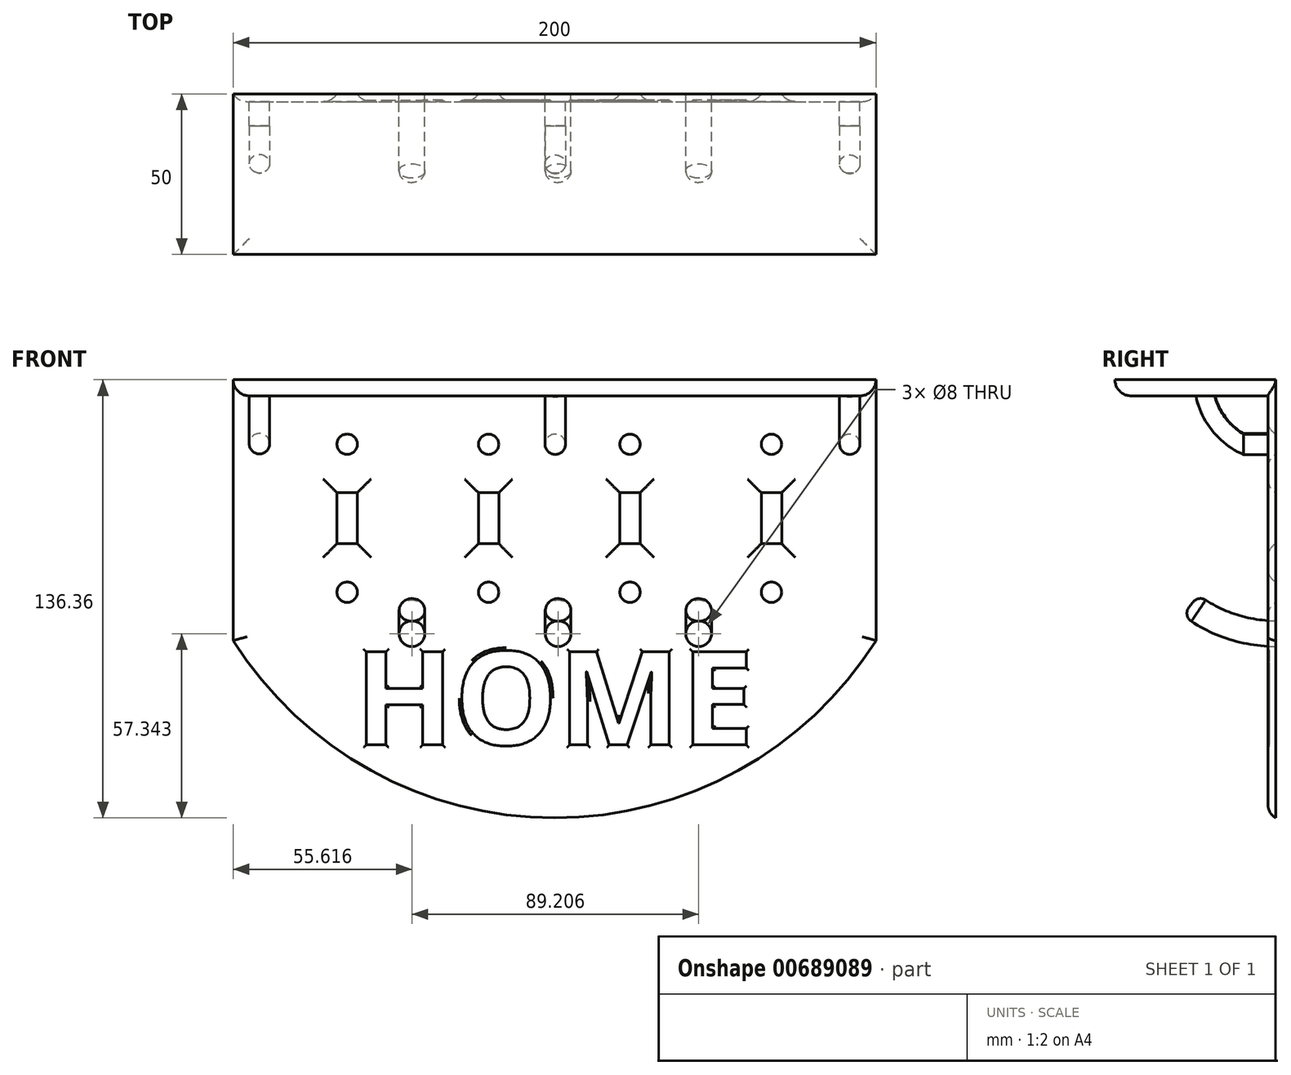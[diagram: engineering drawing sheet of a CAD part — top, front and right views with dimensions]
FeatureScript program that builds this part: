
annotation { "Feature Type Name" : "Feature", "Feature Type Description" : "" }
export const myFeature = defineFeature(function(context is Context, id is Id, definition is map)
    precondition{}
    {
        {
            var Q0;
            Q0=qCreatedBy(makeId("Front.planeOp"),FACE);
            var sketch = newSketch(context, id + "F0", { "sketchPlane" : qUnion([Q0])});
            skLineSegment(sketch, "E0.bottom", {"start": v(-79.45, 38.1) * mm, "end": v(120.55, 38.1) * mm});
            skLineSegment(sketch, "E0.left", {"start": v(-79.45, 38.1) * mm, "end": v(-79.45, -38.1) * mm});
            skLineSegment(sketch, "E0.right", {"start": v(120.55, 38.1) * mm, "end": v(120.55, -38.1) * mm});
            skLineSegment(sketch, "E1.bottom", {"start": v(3.18, 7.94) * mm, "end": v(-3.17, 7.94) * mm});
            skLineSegment(sketch, "E1.top", {"start": v(3.17, -7.94) * mm, "end": v(-3.18, -7.94) * mm});
            skLineSegment(sketch, "E1.left", {"start": v(3.18, 7.94) * mm, "end": v(3.17, -7.94) * mm});
            skLineSegment(sketch, "E1.right", {"start": v(-3.17, 7.94) * mm, "end": v(-3.18, -7.94) * mm});
            skPoint(sketch, "E1.middle", {"position": v(0, 0) * mm});
            skCircle(sketch, "E2", {"center": v(0, 23.03) * mm, "radius": 3.18 * mm});
            skLineSegment(sketch, "E3.bottom", {"start": v(-47.17, 7.94) * mm, "end": v(-40.83, 7.94) * mm});
            skLineSegment(sketch, "E3.top", {"start": v(-47.17, -7.94) * mm, "end": v(-40.83, -7.94) * mm});
            skLineSegment(sketch, "E3.left", {"start": v(-47.17, 7.94) * mm, "end": v(-47.17, -7.94) * mm});
            skLineSegment(sketch, "E3.right", {"start": v(-40.83, 7.94) * mm, "end": v(-40.83, -7.94) * mm});
            skPoint(sketch, "E3.middle", {"position": v(-44, 0) * mm});
            skLineSegment(sketch, "E4.bottom", {"start": v(84.83, 7.94) * mm, "end": v(91.18, 7.94) * mm});
            skLineSegment(sketch, "E4.top", {"start": v(84.83, -7.94) * mm, "end": v(91.18, -7.94) * mm});
            skLineSegment(sketch, "E4.left", {"start": v(84.83, 7.94) * mm, "end": v(84.83, -7.94) * mm});
            skLineSegment(sketch, "E4.right", {"start": v(91.18, 7.94) * mm, "end": v(91.18, -7.94) * mm});
            skPoint(sketch, "E4.middle", {"position": v(88, 0) * mm});
            skCircle(sketch, "E5", {"center": v(-44, 23.04) * mm, "radius": 3.18 * mm});
            skCircle(sketch, "E6", {"center": v(88, 23.03) * mm, "radius": 3.18 * mm});
            skCircle(sketch, "E7", {"center": v(0, -23.03) * mm, "radius": 3.17 * mm});
            skPoint(sketch, "E7.centerSnap0", {"position": v(0, -7.94) * mm});
            skCircle(sketch, "E8", {"center": v(-44, -23.03) * mm, "radius": 3.17 * mm});
            skCircle(sketch, "E9", {"center": v(88, -23.03) * mm, "radius": 3.17 * mm});
            skLineSegment(sketch, "E10.bottom", {"start": v(40.83, 7.94) * mm, "end": v(47.17, 7.94) * mm});
            skLineSegment(sketch, "E10.top", {"start": v(40.83, -7.94) * mm, "end": v(47.17, -7.94) * mm});
            skLineSegment(sketch, "E10.left", {"start": v(40.83, 7.94) * mm, "end": v(40.83, -7.94) * mm});
            skLineSegment(sketch, "E10.right", {"start": v(47.17, 7.94) * mm, "end": v(47.17, -7.94) * mm});
            skPoint(sketch, "E10.middle", {"position": v(44, 0) * mm});
            skCircle(sketch, "E11", {"center": v(44, 23.03) * mm, "radius": 3.18 * mm});
            skCircle(sketch, "E12", {"center": v(44, -23.03) * mm, "radius": 3.17 * mm});
            skArc(sketch, "E13", {"start": v(-79.45, -38.1) * mm, "mid": v(20.55, -93.26) * mm, "end": v(120.55, -38.1) * mm});
            skLineSegment(sketch, "E14.top", {"start": v(-79.45, 43.1) * mm, "end": v(120.55, 43.1) * mm});
            skLineSegment(sketch, "E15.left", {"start": v(-79.45, 38.1) * mm, "end": v(-79.45, 43.1) * mm});
            skLineSegment(sketch, "E15.right", {"start": v(120.55, 38.1) * mm, "end": v(120.55, 43.1) * mm});
            skLineSegment(sketch, "E16.bottom", {"start": v(-79.45, 43.1) * mm, "end": v(-74.45, 43.1) * mm});
            skLineSegment(sketch, "E16.top", {"start": v(-79.45, 43.1) * mm, "end": v(-74.45, 43.1) * mm});
            skLineSegment(sketch, "E17.bottom", {"start": v(120.55, 43.1) * mm, "end": v(115.55, 43.1) * mm});
            skLineSegment(sketch, "E17.top", {"start": v(120.55, 43.1) * mm, "end": v(115.55, 43.1) * mm});
            skLineSegment(sketch, "E18.bottom", {"start": v(20.55, 43.1) * mm, "end": v(18.05, 43.1) * mm});
            skLineSegment(sketch, "E18.top", {"start": v(20.55, 43.1) * mm, "end": v(18.05, 43.1) * mm});
            skCircle(sketch, "E19", {"center": v(-23.83, -35.92) * mm, "radius": 4 * mm});
            skCircle(sketch, "E20", {"center": v(21.64, -35.92) * mm, "radius": 4 * mm});
            skCircle(sketch, "E21", {"center": v(65.37, -35.92) * mm, "radius": 4 * mm});
            skCircle(sketch, "E22", {"center": v(-71.28, 23.2) * mm, "radius": 3.17 * mm});
            skCircle(sketch, "E23", {"center": v(112.37, 23.03) * mm, "radius": 3.18 * mm});
            skCircle(sketch, "E24", {"center": v(20.74, 23.03) * mm, "radius": 3.18 * mm});
            skText(sketch, "E25", { "text": "HOME", "fontName": "OpenSans-Bold.ttf"});
            const initialGuessF0  = {"E25": [-0.0417, -0.07053, 1, 0, 0.0292]};
            skSetInitialGuess(sketch, initialGuessF0);
            skSolve(sketch);
        }
        {
            var Q0;
            Q0=makeQuery(id+"F0.imprint","IMPRINT",FACE,{"disambiguationData":[TD([[makeQuery(id+"F0.imprint","IMPRINT",EDGE,{"derivedFrom":sQuery(id+"F0.wireOp",EDGE,"E0.left")}),1.0]])]});
            var Q1;
            Q1=makeQuery(id+"F0.imprint","IMPRINT",FACE,{"disambiguationData":[TD([[makeQuery(id+"F0.imprint","IMPRINT",EDGE,{"derivedFrom":sQuery(id+"F0.wireOp",EDGE,"E25.sketch_text.stroke-20")}),1.0]])]});
            extrude(context, id + "F1", {"entities" : qUnion([Q0, Q1]), "depth" : 2.4 * mm, "offsetDistance" : 25 * mm});
        }
        {
            var Q0;
            Q0=makeQuery(id+"F0.imprint","IMPRINT",FACE,{"disambiguationData":[TD([[makeQuery(id+"F0.imprint","IMPRINT",EDGE,{"derivedFrom":sQuery(id+"F0.wireOp",EDGE,"E0.bottom")}),1.0]])]});
            extrude(context, id + "F2", {"entities" : qUnion([Q0]), "operationType" : NewBodyOperationType.ADD, "depth" : 50 * mm, "offsetDistance" : 25 * mm});
        }
        {
            var Q0;
            Q0=makeQuery(id+"F0.imprint","IMPRINT",FACE,{"disambiguationData":[TD([[makeQuery(id+"F0.imprint","IMPRINT",EDGE,{"derivedFrom":sQuery(id+"F0.wireOp",EDGE,"E19")}),1.0]])]});
            var Q1;
            Q1=makeQuery(id+"F0.imprint","IMPRINT",FACE,{"disambiguationData":[TD([[makeQuery(id+"F0.imprint","IMPRINT",EDGE,{"derivedFrom":sQuery(id+"F0.wireOp",EDGE,"E20")}),1.0]])]});
            var Q2;
            Q2=makeQuery(id+"F0.imprint","IMPRINT",FACE,{"disambiguationData":[TD([[makeQuery(id+"F0.imprint","IMPRINT",EDGE,{"derivedFrom":sQuery(id+"F0.wireOp",EDGE,"E21")}),1.0]])]});
            var Q3;
            Q3=sQuery(id+"F0.wireOp",EDGE,"E3.bottom");
            revolve(context, id + "F3", {"surfaceOperationType" : NewSurfaceOperationType.NEW, "entities" : qUnion([Q0, Q1, Q2]), "axis" : qUnion([Q3]), "revolveType" : RevolveType.ONE_DIRECTION, "oppositeDirection" : true, "angle" : 37.1 * degree});
        }
        {
            var Q0;
            Q0=makeQuery(id+"F0.imprint","IMPRINT",FACE,{"disambiguationData":[TD([[makeQuery(id+"F0.imprint","IMPRINT",EDGE,{"derivedFrom":sQuery(id+"F0.wireOp",EDGE,"E22")}),1.0]])]});
            var Q1;
            Q1=makeQuery(id+"F0.imprint","IMPRINT",FACE,{"disambiguationData":[TD([[makeQuery(id+"F0.imprint","IMPRINT",EDGE,{"derivedFrom":sQuery(id+"F0.wireOp",EDGE,"E24")}),1.0]])]});
            var Q2;
            Q2=makeQuery(id+"F0.imprint","IMPRINT",FACE,{"disambiguationData":[TD([[makeQuery(id+"F0.imprint","IMPRINT",EDGE,{"derivedFrom":sQuery(id+"F0.wireOp",EDGE,"E23")}),1.0]])]});
            extrude(context, id + "F4", {"entities" : qUnion([Q0, Q1, Q2]), "operationType" : NewBodyOperationType.ADD, "depth" : 10 * mm, "offsetDistance" : 25 * mm});
        }
        {
            var Q0;
            Q0=makeQuery(id+"F4.opExtrude","CAP_FACE",FACE,{"disambiguationData":[OSD([sQuery(id+"F0.wireOp",EDGE,"E22")])],"isStart":false});
            var Q1;
            Q1=makeQuery(id+"F4.opExtrude","CAP_FACE",FACE,{"disambiguationData":[OSD([sQuery(id+"F0.wireOp",EDGE,"E24")])],"isStart":false});
            var Q2;
            Q2=makeQuery(id+"F4.opExtrude","CAP_FACE",FACE,{"disambiguationData":[OSD([sQuery(id+"F0.wireOp",EDGE,"E23")])],"isStart":false});
            var Q3;
            Q3=sQuery(id+"F0.wireOp",EDGE,"E14.top");
            revolve(context, id + "F5", {"operationType" : NewBodyOperationType.ADD, "surfaceOperationType" : NewSurfaceOperationType.NEW, "entities" : qUnion([Q0, Q1, Q2]), "axis" : qUnion([Q3]), "revolveType" : RevolveType.ONE_DIRECTION, "oppositeDirection" : true, "angle" : 55 * degree});
        }
        {
            var Q0;
            Q0=makeQuery(id+"F2.opExtrude","SWEPT_EDGE",EDGE,{"disambiguationData":[OSD([sQuery(id+"F0.wireOp",EDGE,"E0.left"),sQuery(id+"F0.wireOp",EDGE,"E0.bottom"),sQuery(id+"F0.wireOp",EDGE,"E15.left")])]});
            var Q1;
            Q1=makeQuery(id+"F2.opExtrude","CAP_EDGE",EDGE,{"disambiguationData":[OSD([sQuery(id+"F0.wireOp",EDGE,"E0.bottom")])],"isStart":false});
            var Q2;
            Q2=makeQuery(id+"F2.opExtrude","SWEPT_EDGE",EDGE,{"disambiguationData":[OSD([sQuery(id+"F0.wireOp",EDGE,"E0.right"),sQuery(id+"F0.wireOp",EDGE,"E0.bottom"),sQuery(id+"F0.wireOp",EDGE,"E15.right")])]});
            fillet(context, id + "F6", {"entities" : qUnion([Q0, Q1, Q2]), "radius" : 5 * mm, "tangentPropagation" : true, "allowEdgeOverflow" : false});
        }
        {
            var Q0;
            Q0=makeQuery(id+"F1.opExtrude","CAP_EDGE",EDGE,{"disambiguationData":[OSD([sQuery(id+"F0.wireOp",EDGE,"E0.left")])],"isStart":false});
            var Q1;
            Q1=makeQuery(id+"F1.opExtrude","CAP_EDGE",EDGE,{"disambiguationData":[OSD([sQuery(id+"F0.wireOp",EDGE,"E0.right")])],"isStart":false});
            var Q2;
            Q2=makeQuery(id+"F1.opExtrude","CAP_EDGE",EDGE,{"disambiguationData":[OSD([sQuery(id+"F0.wireOp",EDGE,"E13")])],"isStart":false});
            var Q3;
            Q3=makeQuery(id+"F1.opExtrude","CAP_EDGE",EDGE,{"disambiguationData":[OSD([sQuery(id+"F0.wireOp",EDGE,"E3.right")])],"isStart":false});
            var Q4;
            Q4=makeQuery(id+"F1.opExtrude","CAP_EDGE",EDGE,{"disambiguationData":[OSD([sQuery(id+"F0.wireOp",EDGE,"E3.left")])],"isStart":false});
            var Q5;
            Q5=makeQuery(id+"F1.opExtrude","CAP_EDGE",EDGE,{"disambiguationData":[OSD([sQuery(id+"F0.wireOp",EDGE,"E3.bottom")])],"isStart":false});
            var Q6;
            Q6=makeQuery(id+"F1.opExtrude","CAP_EDGE",EDGE,{"disambiguationData":[OSD([sQuery(id+"F0.wireOp",EDGE,"E3.top")])],"isStart":false});
            var Q7;
            Q7=makeQuery(id+"F1.opExtrude","CAP_EDGE",EDGE,{"disambiguationData":[OSD([sQuery(id+"F0.wireOp",EDGE,"E1.right")])],"isStart":false});
            var Q8;
            Q8=makeQuery(id+"F1.opExtrude","CAP_EDGE",EDGE,{"disambiguationData":[OSD([sQuery(id+"F0.wireOp",EDGE,"E1.bottom")])],"isStart":false});
            var Q9;
            Q9=makeQuery(id+"F1.opExtrude","CAP_EDGE",EDGE,{"disambiguationData":[OSD([sQuery(id+"F0.wireOp",EDGE,"E1.left")])],"isStart":false});
            var Q10;
            Q10=makeQuery(id+"F1.opExtrude","CAP_EDGE",EDGE,{"disambiguationData":[OSD([sQuery(id+"F0.wireOp",EDGE,"E1.top")])],"isStart":false});
            var Q11;
            Q11=makeQuery(id+"F1.opExtrude","CAP_EDGE",EDGE,{"disambiguationData":[OSD([sQuery(id+"F0.wireOp",EDGE,"E10.left")])],"isStart":false});
            var Q12;
            Q12=makeQuery(id+"F1.opExtrude","CAP_EDGE",EDGE,{"disambiguationData":[OSD([sQuery(id+"F0.wireOp",EDGE,"E10.bottom")])],"isStart":false});
            var Q13;
            Q13=makeQuery(id+"F1.opExtrude","CAP_EDGE",EDGE,{"disambiguationData":[OSD([sQuery(id+"F0.wireOp",EDGE,"E10.right")])],"isStart":false});
            var Q14;
            Q14=makeQuery(id+"F1.opExtrude","CAP_EDGE",EDGE,{"disambiguationData":[OSD([sQuery(id+"F0.wireOp",EDGE,"E10.top")])],"isStart":false});
            var Q15;
            Q15=makeQuery(id+"F1.opExtrude","CAP_EDGE",EDGE,{"disambiguationData":[OSD([sQuery(id+"F0.wireOp",EDGE,"E4.left")])],"isStart":false});
            var Q16;
            Q16=makeQuery(id+"F1.opExtrude","CAP_EDGE",EDGE,{"disambiguationData":[OSD([sQuery(id+"F0.wireOp",EDGE,"E4.bottom")])],"isStart":false});
            var Q17;
            Q17=makeQuery(id+"F1.opExtrude","CAP_EDGE",EDGE,{"disambiguationData":[OSD([sQuery(id+"F0.wireOp",EDGE,"E4.right")])],"isStart":false});
            var Q18;
            Q18=makeQuery(id+"F1.opExtrude","CAP_EDGE",EDGE,{"disambiguationData":[OSD([sQuery(id+"F0.wireOp",EDGE,"E4.top")])],"isStart":false});
            var Q19;
            Q19=makeQuery(id+"F1.opExtrude","CAP_EDGE",EDGE,{"disambiguationData":[OSD([sQuery(id+"F0.wireOp",EDGE,"E9")])],"isStart":false});
            var Q20;
            Q20=makeQuery(id+"F1.opExtrude","CAP_EDGE",EDGE,{"disambiguationData":[OSD([sQuery(id+"F0.wireOp",EDGE,"E6")])],"isStart":false});
            var Q21;
            Q21=makeQuery(id+"F1.opExtrude","CAP_EDGE",EDGE,{"disambiguationData":[OSD([sQuery(id+"F0.wireOp",EDGE,"E12")])],"isStart":false});
            var Q22;
            Q22=makeQuery(id+"F1.opExtrude","CAP_EDGE",EDGE,{"disambiguationData":[OSD([sQuery(id+"F0.wireOp",EDGE,"E11")])],"isStart":false});
            var Q23;
            Q23=makeQuery(id+"F1.opExtrude","CAP_EDGE",EDGE,{"disambiguationData":[OSD([sQuery(id+"F0.wireOp",EDGE,"E7")])],"isStart":false});
            var Q24;
            Q24=makeQuery(id+"F1.opExtrude","CAP_EDGE",EDGE,{"disambiguationData":[OSD([sQuery(id+"F0.wireOp",EDGE,"E2")])],"isStart":false});
            var Q25;
            Q25=makeQuery(id+"F1.opExtrude","CAP_EDGE",EDGE,{"disambiguationData":[OSD([sQuery(id+"F0.wireOp",EDGE,"E8")])],"isStart":false});
            var Q26;
            Q26=makeQuery(id+"F1.opExtrude","CAP_EDGE",EDGE,{"disambiguationData":[OSD([sQuery(id+"F0.wireOp",EDGE,"E5")])],"isStart":false});
            fillet(context, id + "F7", {"entities" : qUnion([Q0, Q1, Q2, Q3, Q4, Q5, Q6, Q7, Q8, Q9, Q10, Q11, Q12, Q13, Q14, Q15, Q16, Q17, Q18, Q19, Q20, Q21, Q22, Q23, Q24, Q25, Q26]), "radius" : 5 * mm, "tangentPropagation" : true, "allowEdgeOverflow" : false});
        }
        {
            var Q0;
            Q0=makeQuery(id+"F3.opRevolve","CAP_EDGE",EDGE,{"disambiguationData":[OSD([sQuery(id+"F0.wireOp",EDGE,"E19")])],"isStart":false});
            var Q1;
            Q1=makeQuery(id+"F3.opRevolve","CAP_EDGE",EDGE,{"disambiguationData":[OSD([sQuery(id+"F0.wireOp",EDGE,"E20")])],"isStart":false});
            var Q2;
            Q2=makeQuery(id+"F3.opRevolve","CAP_EDGE",EDGE,{"disambiguationData":[OSD([sQuery(id+"F0.wireOp",EDGE,"E21")])],"isStart":false});
            fillet(context, id + "F8", {"entities" : qUnion([Q0, Q1, Q2]), "radius" : 3 * mm, "tangentPropagation" : true, "allowEdgeOverflow" : false});
        }
        {
            var Q0;
            Q0=makeQuery(id+"F0.imprint","IMPRINT",FACE,{"disambiguationData":[TD([[makeQuery(id+"F0.imprint","IMPRINT",EDGE,{"derivedFrom":sQuery(id+"F0.wireOp",EDGE,"E25.sketch_text.stroke-0")}),-1.0]])]});
            var Q1;
            Q1=makeQuery(id+"F0.imprint","IMPRINT",FACE,{"disambiguationData":[TD([[makeQuery(id+"F0.imprint","IMPRINT",EDGE,{"derivedFrom":sQuery(id+"F0.wireOp",EDGE,"E25.sketch_text.stroke-12")}),-1.0]])]});
            var Q2;
            Q2=makeQuery(id+"F0.imprint","IMPRINT",FACE,{"disambiguationData":[TD([[makeQuery(id+"F0.imprint","IMPRINT",EDGE,{"derivedFrom":sQuery(id+"F0.wireOp",EDGE,"E25.sketch_text.stroke-26")}),-1.0]])]});
            var Q3;
            Q3=makeQuery(id+"F0.imprint","IMPRINT",FACE,{"disambiguationData":[TD([[makeQuery(id+"F0.imprint","IMPRINT",EDGE,{"derivedFrom":sQuery(id+"F0.wireOp",EDGE,"E25.sketch_text.stroke-45")}),-1.0]])]});
            extrude(context, id + "F9", {"entities" : qUnion([Q0, Q1, Q2, Q3]), "operationType" : NewBodyOperationType.ADD, "depth" : 2 * mm, "offsetDistance" : 25 * mm});
        }
        {
            var Q0;
            Q0=makeQuery(id+"F1.opExtrude","CAP_EDGE",EDGE,{"disambiguationData":[OSD([sQuery(id+"F0.wireOp",EDGE,"E25.sketch_text.stroke-12")])],"isStart":false});
            var Q1;
            Q1=makeQuery(id+"F1.opExtrude","CAP_EDGE",EDGE,{"disambiguationData":[OSD([sQuery(id+"F0.wireOp",EDGE,"E25.sketch_text.stroke-25")])],"isStart":false});
            var Q2;
            Q2=makeQuery(id+"F1.opExtrude","CAP_EDGE",EDGE,{"disambiguationData":[OSD([sQuery(id+"F0.wireOp",EDGE,"E25.sketch_text.stroke-5")])],"isStart":false});
            var Q3;
            Q3=makeQuery(id+"F1.opExtrude","CAP_EDGE",EDGE,{"disambiguationData":[OSD([sQuery(id+"F0.wireOp",EDGE,"E25.sketch_text.stroke-11")])],"isStart":false});
            var Q4;
            Q4=makeQuery(id+"F1.opExtrude","CAP_EDGE",EDGE,{"disambiguationData":[OSD([sQuery(id+"F0.wireOp",EDGE,"E25.sketch_text.stroke-10")])],"isStart":false});
            var Q5;
            Q5=makeQuery(id+"F1.opExtrude","CAP_EDGE",EDGE,{"disambiguationData":[OSD([sQuery(id+"F0.wireOp",EDGE,"E25.sketch_text.stroke-9")])],"isStart":false});
            var Q6;
            Q6=makeQuery(id+"F1.opExtrude","CAP_EDGE",EDGE,{"disambiguationData":[OSD([sQuery(id+"F0.wireOp",EDGE,"E25.sketch_text.stroke-7")])],"isStart":false});
            var Q7;
            Q7=makeQuery(id+"F1.opExtrude","CAP_EDGE",EDGE,{"disambiguationData":[OSD([sQuery(id+"F0.wireOp",EDGE,"E25.sketch_text.stroke-8")])],"isStart":false});
            var Q8;
            Q8=makeQuery(id+"F1.opExtrude","CAP_EDGE",EDGE,{"disambiguationData":[OSD([sQuery(id+"F0.wireOp",EDGE,"E25.sketch_text.stroke-3")])],"isStart":false});
            var Q9;
            Q9=makeQuery(id+"F1.opExtrude","CAP_EDGE",EDGE,{"disambiguationData":[OSD([sQuery(id+"F0.wireOp",EDGE,"E25.sketch_text.stroke-4")])],"isStart":false});
            var Q10;
            Q10=makeQuery(id+"F1.opExtrude","CAP_EDGE",EDGE,{"disambiguationData":[OSD([sQuery(id+"F0.wireOp",EDGE,"E25.sketch_text.stroke-2")])],"isStart":false});
            var Q11;
            Q11=makeQuery(id+"F1.opExtrude","CAP_EDGE",EDGE,{"disambiguationData":[OSD([sQuery(id+"F0.wireOp",EDGE,"E25.sketch_text.stroke-6")])],"isStart":false});
            var Q12;
            Q12=makeQuery(id+"F1.opExtrude","CAP_EDGE",EDGE,{"disambiguationData":[OSD([sQuery(id+"F0.wireOp",EDGE,"E25.sketch_text.stroke-1")])],"isStart":false});
            var Q13;
            Q13=makeQuery(id+"F1.opExtrude","CAP_EDGE",EDGE,{"disambiguationData":[OSD([sQuery(id+"F0.wireOp",EDGE,"E25.sketch_text.stroke-0")])],"isStart":false});
            var Q14;
            Q14=makeQuery(id+"F1.opExtrude","CAP_EDGE",EDGE,{"disambiguationData":[OSD([sQuery(id+"F0.wireOp",EDGE,"E25.sketch_text.stroke-30")])],"isStart":false});
            var Q15;
            Q15=makeQuery(id+"F1.opExtrude","CAP_EDGE",EDGE,{"disambiguationData":[OSD([sQuery(id+"F0.wireOp",EDGE,"E25.sketch_text.stroke-31")])],"isStart":false});
            var Q16;
            Q16=makeQuery(id+"F1.opExtrude","CAP_EDGE",EDGE,{"disambiguationData":[OSD([sQuery(id+"F0.wireOp",EDGE,"E25.sketch_text.stroke-32")])],"isStart":false});
            var Q17;
            Q17=makeQuery(id+"F1.opExtrude","CAP_EDGE",EDGE,{"disambiguationData":[OSD([sQuery(id+"F0.wireOp",EDGE,"E25.sketch_text.stroke-33")])],"isStart":false});
            var Q18;
            Q18=makeQuery(id+"F1.opExtrude","CAP_EDGE",EDGE,{"disambiguationData":[OSD([sQuery(id+"F0.wireOp",EDGE,"E25.sketch_text.stroke-26")])],"isStart":false});
            var Q19;
            Q19=makeQuery(id+"F1.opExtrude","CAP_EDGE",EDGE,{"disambiguationData":[OSD([sQuery(id+"F0.wireOp",EDGE,"E25.sketch_text.stroke-29")])],"isStart":false});
            var Q20;
            Q20=makeQuery(id+"F1.opExtrude","CAP_EDGE",EDGE,{"disambiguationData":[OSD([sQuery(id+"F0.wireOp",EDGE,"E25.sketch_text.stroke-43")])],"isStart":false});
            var Q21;
            Q21=makeQuery(id+"F1.opExtrude","CAP_EDGE",EDGE,{"disambiguationData":[OSD([sQuery(id+"F0.wireOp",EDGE,"E25.sketch_text.stroke-37")])],"isStart":false});
            var Q22;
            Q22=makeQuery(id+"F1.opExtrude","CAP_EDGE",EDGE,{"disambiguationData":[OSD([sQuery(id+"F0.wireOp",EDGE,"E25.sketch_text.stroke-36")])],"isStart":false});
            var Q23;
            Q23=makeQuery(id+"F1.opExtrude","CAP_EDGE",EDGE,{"disambiguationData":[OSD([sQuery(id+"F0.wireOp",EDGE,"E25.sketch_text.stroke-35")])],"isStart":false});
            var Q24;
            Q24=makeQuery(id+"F1.opExtrude","CAP_EDGE",EDGE,{"disambiguationData":[OSD([sQuery(id+"F0.wireOp",EDGE,"E25.sketch_text.stroke-39")])],"isStart":false});
            var Q25;
            Q25=makeQuery(id+"F1.opExtrude","CAP_EDGE",EDGE,{"disambiguationData":[OSD([sQuery(id+"F0.wireOp",EDGE,"E25.sketch_text.stroke-44")])],"isStart":false});
            var Q26;
            Q26=makeQuery(id+"F1.opExtrude","CAP_EDGE",EDGE,{"disambiguationData":[OSD([sQuery(id+"F0.wireOp",EDGE,"E25.sketch_text.stroke-38")])],"isStart":false});
            var Q27;
            Q27=makeQuery(id+"F1.opExtrude","CAP_EDGE",EDGE,{"disambiguationData":[OSD([sQuery(id+"F0.wireOp",EDGE,"E25.sketch_text.stroke-46")])],"isStart":false});
            var Q28;
            Q28=makeQuery(id+"F1.opExtrude","CAP_EDGE",EDGE,{"disambiguationData":[OSD([sQuery(id+"F0.wireOp",EDGE,"E25.sketch_text.stroke-54")])],"isStart":false});
            var Q29;
            Q29=makeQuery(id+"F1.opExtrude","CAP_EDGE",EDGE,{"disambiguationData":[OSD([sQuery(id+"F0.wireOp",EDGE,"E25.sketch_text.stroke-50")])],"isStart":false});
            var Q30;
            Q30=makeQuery(id+"F1.opExtrude","CAP_EDGE",EDGE,{"disambiguationData":[OSD([sQuery(id+"F0.wireOp",EDGE,"E25.sketch_text.stroke-47")])],"isStart":false});
            var Q31;
            Q31=makeQuery(id+"F1.opExtrude","CAP_EDGE",EDGE,{"disambiguationData":[OSD([sQuery(id+"F0.wireOp",EDGE,"E25.sketch_text.stroke-48")])],"isStart":false});
            var Q32;
            Q32=makeQuery(id+"F1.opExtrude","CAP_EDGE",EDGE,{"disambiguationData":[OSD([sQuery(id+"F0.wireOp",EDGE,"E25.sketch_text.stroke-51")])],"isStart":false});
            var Q33;
            Q33=makeQuery(id+"F1.opExtrude","CAP_EDGE",EDGE,{"disambiguationData":[OSD([sQuery(id+"F0.wireOp",EDGE,"E25.sketch_text.stroke-49")])],"isStart":false});
            var Q34;
            Q34=makeQuery(id+"F1.opExtrude","CAP_EDGE",EDGE,{"disambiguationData":[OSD([sQuery(id+"F0.wireOp",EDGE,"E25.sketch_text.stroke-53")])],"isStart":false});
            var Q35;
            Q35=makeQuery(id+"F1.opExtrude","CAP_EDGE",EDGE,{"disambiguationData":[OSD([sQuery(id+"F0.wireOp",EDGE,"E25.sketch_text.stroke-55")])],"isStart":false});
            var Q36;
            Q36=makeQuery(id+"F1.opExtrude","CAP_EDGE",EDGE,{"disambiguationData":[OSD([sQuery(id+"F0.wireOp",EDGE,"E25.sketch_text.stroke-56")])],"isStart":false});
            var Q37;
            Q37=makeQuery(id+"F1.opExtrude","CAP_EDGE",EDGE,{"disambiguationData":[OSD([sQuery(id+"F0.wireOp",EDGE,"E25.sketch_text.stroke-52")])],"isStart":false});
            var Q38;
            Q38=makeQuery(id+"F1.opExtrude","CAP_EDGE",EDGE,{"disambiguationData":[OSD([sQuery(id+"F0.wireOp",EDGE,"E25.sketch_text.stroke-45")])],"isStart":false});
            fillet(context, id + "F10", {"entities" : qUnion([Q0, Q1, Q2, Q3, Q4, Q5, Q6, Q7, Q8, Q9, Q10, Q11, Q12, Q13, Q14, Q15, Q16, Q17, Q18, Q19, Q20, Q21, Q22, Q23, Q24, Q25, Q26, Q27, Q28, Q29, Q30, Q31, Q32, Q33, Q34, Q35, Q36, Q37, Q38]), "radius" : 1 * mm, "tangentPropagation" : true, "allowEdgeOverflow" : false});
        }
    });
